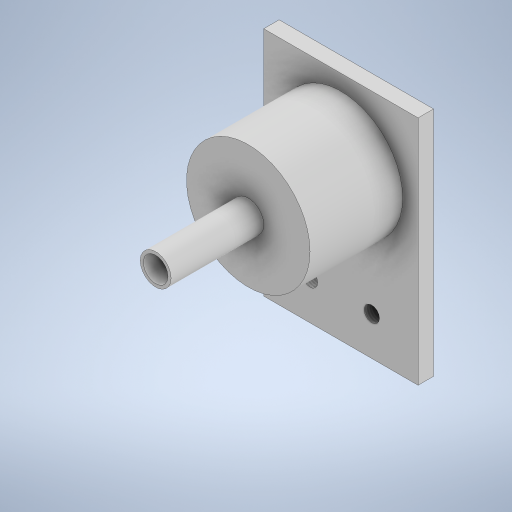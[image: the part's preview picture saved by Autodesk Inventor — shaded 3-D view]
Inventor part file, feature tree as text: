
AUTODESK INVENTOR PART (.ipt)
format: ipt  version: 2024 (Build 280153000, 153)  size: 277,504 bytes
history: native  units: mm
features: extrude x4, sketch x4, thread x2
ambient origin geometry x8: Origin, YZ Plane, XZ Plane, XY Plane, X Axis, Y Axis, Z Axis, Center Point
bodies: Solid1 (feature_tree)
feature tree (10):
  extrude  "Extrusion1"  Depth=75.0mm
  extrude  "Extrusion2"  Depth=5.0mm
  sketch  "Sketch3"  dims[d5=25.0mm d6=30.0mm d7=0.0mm]
  extrude  "Extrusion3"  Depth=30.0mm TaperAngle=0.0deg
  extrude  "Extrusion4"  Depth=10.0mm
  thread  "Thread1"  [1 undecoded]
  thread  "Thread2"  [1 undecoded]
  sketch  "Sketch1"  dims[d0=50.0mm d1=75.0mm]
  sketch  "Sketch2"  dims[d2=5.0mm d3=0.0mm d4=40.0mm]
  sketch  "Sketch4"  dims[d8=8.0mm d9=10.0mm d10=30.0mm d11=0.0mm d12=5.0mm d13=5.0mm d14=15.0mm d15=15.0mm d16=12.5mm d17=12.5mm d18=10.0mm d19=0.0mm d20=5.0mm d21=0.0mm d22=5.0mm d23=0.0mm]
note: 2 required parameter values undecoded (feature->parameter linkage not recoverable at this tier; creation-order binding heuristic only, values carry confidence <= 0.55)
